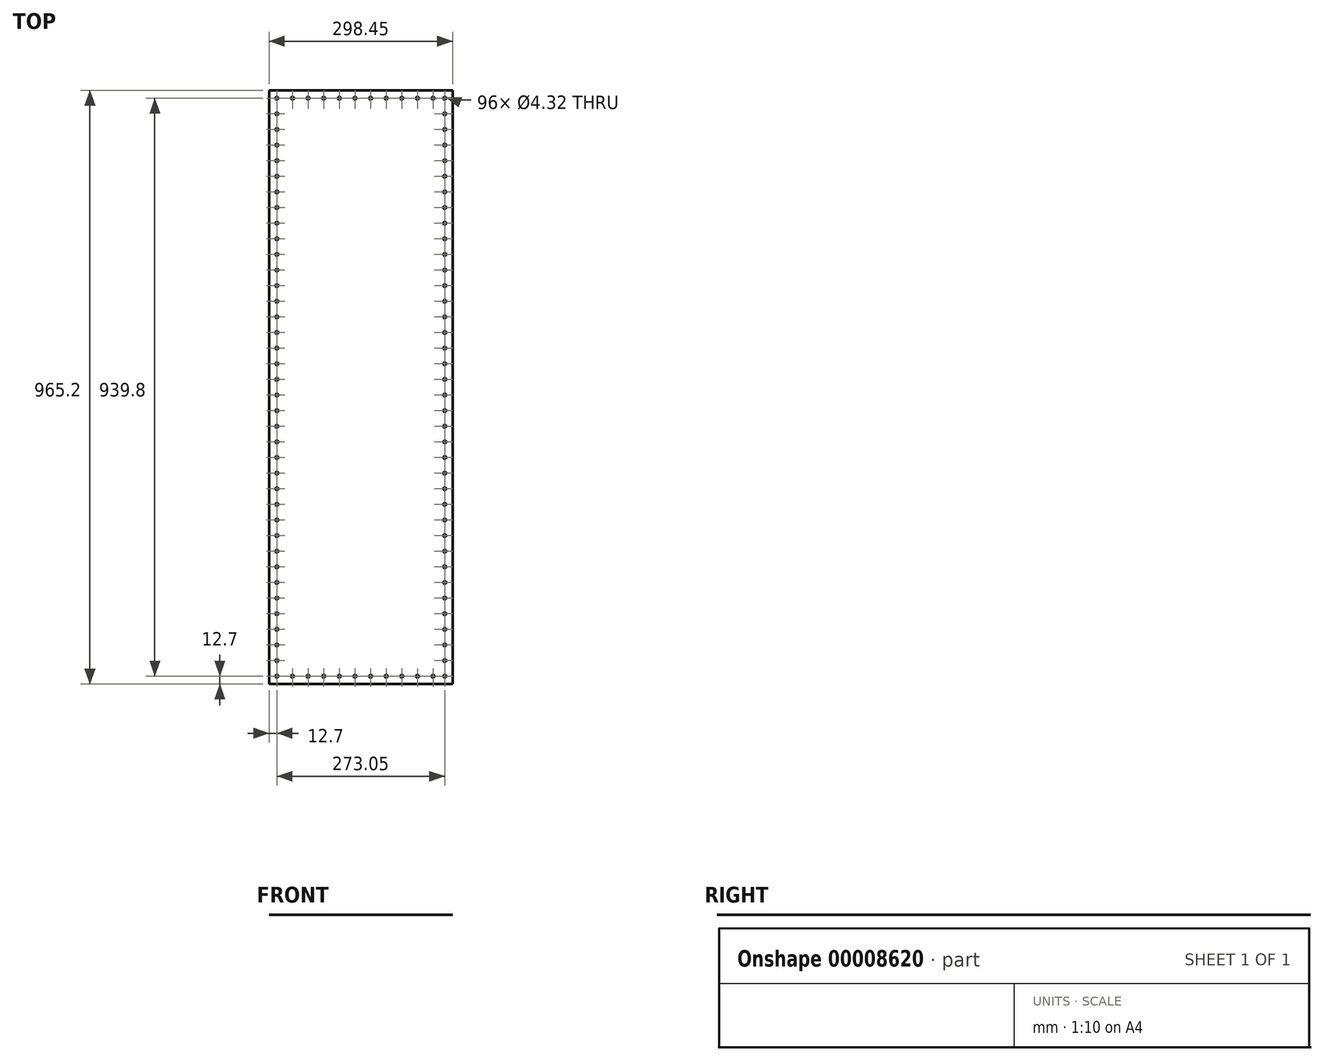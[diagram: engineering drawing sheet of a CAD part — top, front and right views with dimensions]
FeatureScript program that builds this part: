
annotation { "Feature Type Name" : "Feature", "Feature Type Description" : "" }
export const myFeature = defineFeature(function(context is Context, id is Id, definition is map)
    precondition{}
    {
        {
            var Q0;
            Q0=qCreatedBy(makeId("Top.planeOp"),FACE);
            var sketch = newSketch(context, id + "F0", { "sketchPlane" : qUnion([Q0])});
            skLineSegment(sketch, "E0.bottom", {"start": v(0, 0) * mm, "end": v(298.45, 0) * mm});
            skLineSegment(sketch, "E0.top", {"start": v(0, 965.2) * mm, "end": v(298.45, 965.2) * mm});
            skLineSegment(sketch, "E0.left", {"start": v(0, 0) * mm, "end": v(0, 965.2) * mm});
            skLineSegment(sketch, "E0.right", {"start": v(298.45, 0) * mm, "end": v(298.45, 965.2) * mm});
            skSolve(sketch);
        }
        {
            var Q0;
            Q0=makeQuery(id+"F0.imprint","IMPRINT",FACE,{"disambiguationData":[TD([[makeQuery(id+"F0.imprint","IMPRINT",EDGE,{"derivedFrom":sQuery(id+"F0.wireOp",EDGE,"E0.bottom")}),1.0]])]});
            extrude(context, id + "F1", {"entities" : qUnion([Q0]), "depth" : 1 / 203.2 * mm});
        }
        {
            var Q0;
            Q0=makeQuery(id+"F1.opExtrude","CAP_FACE",FACE,{"disambiguationData":[OSD([sQuery(id+"F0.wireOp",EDGE,"E0.bottom"),sQuery(id+"F0.wireOp",EDGE,"E0.top"),sQuery(id+"F0.wireOp",EDGE,"E0.left"),sQuery(id+"F0.wireOp",EDGE,"E0.right")])],"isStart":false});
            var sketch = newSketch(context, id + "F2", { "sketchPlane" : qUnion([Q0])});
            skCircle(sketch, "E1", {"center": v(12.7, 952.5) * mm, "radius": 2.16 * mm});
            skCircle(sketch, "E2.0.1.0", {"center": v(12.7, 927.1) * mm, "radius": 2.16 * mm});
            skCircle(sketch, "E2.0.2.0", {"center": v(12.7, 901.7) * mm, "radius": 2.16 * mm});
            skCircle(sketch, "E2.0.3.0", {"center": v(12.7, 876.3) * mm, "radius": 2.16 * mm});
            skCircle(sketch, "E2.0.4.0", {"center": v(12.7, 850.9) * mm, "radius": 2.16 * mm});
            skCircle(sketch, "E2.0.5.0", {"center": v(12.7, 825.5) * mm, "radius": 2.16 * mm});
            skCircle(sketch, "E2.0.6.0", {"center": v(12.7, 800.1) * mm, "radius": 2.16 * mm});
            skCircle(sketch, "E2.0.7.0", {"center": v(12.7, 774.7) * mm, "radius": 2.16 * mm});
            skCircle(sketch, "E2.0.8.0", {"center": v(12.7, 749.3) * mm, "radius": 2.16 * mm});
            skCircle(sketch, "E2.0.9.0", {"center": v(12.7, 723.9) * mm, "radius": 2.16 * mm});
            skCircle(sketch, "E2.0.10.0", {"center": v(12.7, 698.5) * mm, "radius": 2.16 * mm});
            skCircle(sketch, "E2.0.11.0", {"center": v(12.7, 673.1) * mm, "radius": 2.16 * mm});
            skCircle(sketch, "E2.0.12.0", {"center": v(12.7, 647.7) * mm, "radius": 2.16 * mm});
            skCircle(sketch, "E2.0.13.0", {"center": v(12.7, 622.3) * mm, "radius": 2.16 * mm});
            skCircle(sketch, "E2.0.14.0", {"center": v(12.7, 596.9) * mm, "radius": 2.16 * mm});
            skCircle(sketch, "E2.0.15.0", {"center": v(12.7, 571.5) * mm, "radius": 2.16 * mm});
            skCircle(sketch, "E2.0.16.0", {"center": v(12.7, 546.1) * mm, "radius": 2.16 * mm});
            skCircle(sketch, "E2.0.17.0", {"center": v(12.7, 520.7) * mm, "radius": 2.16 * mm});
            skCircle(sketch, "E2.0.18.0", {"center": v(12.7, 495.3) * mm, "radius": 2.16 * mm});
            skCircle(sketch, "E2.0.19.0", {"center": v(12.7, 469.9) * mm, "radius": 2.16 * mm});
            skCircle(sketch, "E2.0.20.0", {"center": v(12.7, 444.5) * mm, "radius": 2.16 * mm});
            skCircle(sketch, "E2.0.21.0", {"center": v(12.7, 419.1) * mm, "radius": 2.16 * mm});
            skCircle(sketch, "E2.0.22.0", {"center": v(12.7, 393.7) * mm, "radius": 2.16 * mm});
            skCircle(sketch, "E2.0.23.0", {"center": v(12.7, 368.3) * mm, "radius": 2.16 * mm});
            skCircle(sketch, "E2.0.24.0", {"center": v(12.7, 342.9) * mm, "radius": 2.16 * mm});
            skCircle(sketch, "E2.0.25.0", {"center": v(12.7, 317.5) * mm, "radius": 2.16 * mm});
            skCircle(sketch, "E2.0.26.0", {"center": v(12.7, 292.1) * mm, "radius": 2.16 * mm});
            skCircle(sketch, "E2.0.27.0", {"center": v(12.7, 266.7) * mm, "radius": 2.16 * mm});
            skCircle(sketch, "E2.0.28.0", {"center": v(12.7, 241.3) * mm, "radius": 2.16 * mm});
            skCircle(sketch, "E2.0.29.0", {"center": v(12.7, 215.9) * mm, "radius": 2.16 * mm});
            skCircle(sketch, "E2.0.30.0", {"center": v(12.7, 190.5) * mm, "radius": 2.16 * mm});
            skCircle(sketch, "E2.0.31.0", {"center": v(12.7, 165.1) * mm, "radius": 2.16 * mm});
            skCircle(sketch, "E2.0.32.0", {"center": v(12.7, 139.7) * mm, "radius": 2.16 * mm});
            skCircle(sketch, "E2.0.33.0", {"center": v(12.7, 114.3) * mm, "radius": 2.16 * mm});
            skCircle(sketch, "E2.0.34.0", {"center": v(12.7, 88.9) * mm, "radius": 2.16 * mm});
            skCircle(sketch, "E2.0.35.0", {"center": v(12.7, 63.5) * mm, "radius": 2.16 * mm});
            skCircle(sketch, "E2.0.36.0", {"center": v(12.7, 38.1) * mm, "radius": 2.16 * mm});
            skCircle(sketch, "E2.0.37.0", {"center": v(12.7, 12.7) * mm, "radius": 2.16 * mm});
            skLineSegment(sketch, "E2.direction1", {"start": v(12.7, 952.5) * mm, "end": v(38.1, 952.5) * mm, "construction": true});
            skLineSegment(sketch, "E2.direction2", {"start": v(12.7, 952.5) * mm, "end": v(12.7, 927.1) * mm, "construction": true});
            skCircle(sketch, "E3.1.0.0", {"center": v(38.1, 952.5) * mm, "radius": 2.16 * mm});
            skCircle(sketch, "E3.2.0.0", {"center": v(63.5, 952.5) * mm, "radius": 2.16 * mm});
            skCircle(sketch, "E3.3.0.0", {"center": v(88.9, 952.5) * mm, "radius": 2.16 * mm});
            skCircle(sketch, "E3.4.0.0", {"center": v(114.3, 952.5) * mm, "radius": 2.16 * mm});
            skCircle(sketch, "E3.5.0.0", {"center": v(139.7, 952.5) * mm, "radius": 2.16 * mm});
            skCircle(sketch, "E3.6.0.0", {"center": v(165.1, 952.5) * mm, "radius": 2.16 * mm});
            skCircle(sketch, "E3.7.0.0", {"center": v(190.5, 952.5) * mm, "radius": 2.16 * mm});
            skCircle(sketch, "E3.8.0.0", {"center": v(215.9, 952.5) * mm, "radius": 2.16 * mm});
            skCircle(sketch, "E3.9.0.0", {"center": v(241.3, 952.5) * mm, "radius": 2.16 * mm});
            skCircle(sketch, "E3.10.0.0", {"center": v(266.7, 952.5) * mm, "radius": 2.16 * mm});
            skCircle(sketch, "E4.1.0.0", {"center": v(38.1, 12.7) * mm, "radius": 2.16 * mm});
            skCircle(sketch, "E4.2.0.0", {"center": v(63.5, 12.7) * mm, "radius": 2.16 * mm});
            skCircle(sketch, "E4.3.0.0", {"center": v(88.9, 12.7) * mm, "radius": 2.16 * mm});
            skCircle(sketch, "E4.4.0.0", {"center": v(114.3, 12.7) * mm, "radius": 2.16 * mm});
            skCircle(sketch, "E4.5.0.0", {"center": v(139.7, 12.7) * mm, "radius": 2.16 * mm});
            skCircle(sketch, "E4.6.0.0", {"center": v(165.1, 12.7) * mm, "radius": 2.16 * mm});
            skCircle(sketch, "E4.7.0.0", {"center": v(190.5, 12.7) * mm, "radius": 2.16 * mm});
            skCircle(sketch, "E4.8.0.0", {"center": v(215.9, 12.7) * mm, "radius": 2.16 * mm});
            skCircle(sketch, "E4.9.0.0", {"center": v(241.3, 12.7) * mm, "radius": 2.16 * mm});
            skCircle(sketch, "E4.10.0.0", {"center": v(266.7, 12.7) * mm, "radius": 2.16 * mm});
            skLineSegment(sketch, "E4.direction1", {"start": v(12.7, 12.7) * mm, "end": v(38.1, 12.7) * mm, "construction": true});
            skCircle(sketch, "E5", {"center": v(285.75, 952.5) * mm, "radius": 2.16 * mm});
            skCircle(sketch, "E6.0.1.0", {"center": v(285.75, 927.1) * mm, "radius": 2.16 * mm});
            skCircle(sketch, "E6.0.2.0", {"center": v(285.75, 901.7) * mm, "radius": 2.16 * mm});
            skCircle(sketch, "E6.0.3.0", {"center": v(285.75, 876.3) * mm, "radius": 2.16 * mm});
            skCircle(sketch, "E6.0.4.0", {"center": v(285.75, 850.9) * mm, "radius": 2.16 * mm});
            skCircle(sketch, "E6.0.5.0", {"center": v(285.75, 825.5) * mm, "radius": 2.16 * mm});
            skCircle(sketch, "E6.0.6.0", {"center": v(285.75, 800.1) * mm, "radius": 2.16 * mm});
            skCircle(sketch, "E6.0.7.0", {"center": v(285.75, 774.7) * mm, "radius": 2.16 * mm});
            skCircle(sketch, "E6.0.8.0", {"center": v(285.75, 749.3) * mm, "radius": 2.16 * mm});
            skCircle(sketch, "E6.0.9.0", {"center": v(285.75, 723.9) * mm, "radius": 2.16 * mm});
            skCircle(sketch, "E6.0.10.0", {"center": v(285.75, 698.5) * mm, "radius": 2.16 * mm});
            skCircle(sketch, "E6.0.11.0", {"center": v(285.75, 673.1) * mm, "radius": 2.16 * mm});
            skCircle(sketch, "E6.0.12.0", {"center": v(285.75, 647.7) * mm, "radius": 2.16 * mm});
            skCircle(sketch, "E6.0.13.0", {"center": v(285.75, 622.3) * mm, "radius": 2.16 * mm});
            skCircle(sketch, "E6.0.14.0", {"center": v(285.75, 596.9) * mm, "radius": 2.16 * mm});
            skCircle(sketch, "E6.0.15.0", {"center": v(285.75, 571.5) * mm, "radius": 2.16 * mm});
            skCircle(sketch, "E6.0.16.0", {"center": v(285.75, 546.1) * mm, "radius": 2.16 * mm});
            skCircle(sketch, "E6.0.17.0", {"center": v(285.75, 520.7) * mm, "radius": 2.16 * mm});
            skCircle(sketch, "E6.0.18.0", {"center": v(285.75, 495.3) * mm, "radius": 2.16 * mm});
            skCircle(sketch, "E6.0.19.0", {"center": v(285.75, 469.9) * mm, "radius": 2.16 * mm});
            skCircle(sketch, "E6.0.20.0", {"center": v(285.75, 444.5) * mm, "radius": 2.16 * mm});
            skCircle(sketch, "E6.0.21.0", {"center": v(285.75, 419.1) * mm, "radius": 2.16 * mm});
            skCircle(sketch, "E6.0.22.0", {"center": v(285.75, 393.7) * mm, "radius": 2.16 * mm});
            skCircle(sketch, "E6.0.23.0", {"center": v(285.75, 368.3) * mm, "radius": 2.16 * mm});
            skCircle(sketch, "E6.0.24.0", {"center": v(285.75, 342.9) * mm, "radius": 2.16 * mm});
            skCircle(sketch, "E6.0.25.0", {"center": v(285.75, 317.5) * mm, "radius": 2.16 * mm});
            skCircle(sketch, "E6.0.26.0", {"center": v(285.75, 292.1) * mm, "radius": 2.16 * mm});
            skCircle(sketch, "E6.0.27.0", {"center": v(285.75, 266.7) * mm, "radius": 2.16 * mm});
            skCircle(sketch, "E6.0.28.0", {"center": v(285.75, 241.3) * mm, "radius": 2.16 * mm});
            skCircle(sketch, "E6.0.29.0", {"center": v(285.75, 215.9) * mm, "radius": 2.16 * mm});
            skCircle(sketch, "E6.0.30.0", {"center": v(285.75, 190.5) * mm, "radius": 2.16 * mm});
            skCircle(sketch, "E6.0.31.0", {"center": v(285.75, 165.1) * mm, "radius": 2.16 * mm});
            skCircle(sketch, "E6.0.32.0", {"center": v(285.75, 139.7) * mm, "radius": 2.16 * mm});
            skCircle(sketch, "E6.0.33.0", {"center": v(285.75, 114.3) * mm, "radius": 2.16 * mm});
            skCircle(sketch, "E6.0.34.0", {"center": v(285.75, 88.9) * mm, "radius": 2.16 * mm});
            skCircle(sketch, "E6.0.35.0", {"center": v(285.75, 63.5) * mm, "radius": 2.16 * mm});
            skCircle(sketch, "E6.0.36.0", {"center": v(285.75, 38.1) * mm, "radius": 2.16 * mm});
            skCircle(sketch, "E6.0.37.0", {"center": v(285.75, 12.7) * mm, "radius": 2.16 * mm});
            skLineSegment(sketch, "E6.direction1", {"start": v(285.75, 952.5) * mm, "end": v(311.15, 952.5) * mm, "construction": true});
            skLineSegment(sketch, "E6.direction2", {"start": v(285.75, 952.5) * mm, "end": v(285.75, 927.1) * mm, "construction": true});
            skSolve(sketch);
        }
        {
            var Q0;
            Q0 = qSketchRegion(id + "F2", true);
            extrude(context, id + "F3", {"entities" : qUnion([Q0]), "operationType" : NewBodyOperationType.REMOVE, "oppositeDirection" : true, "depth" : 25.4 * mm});
        }
    });
